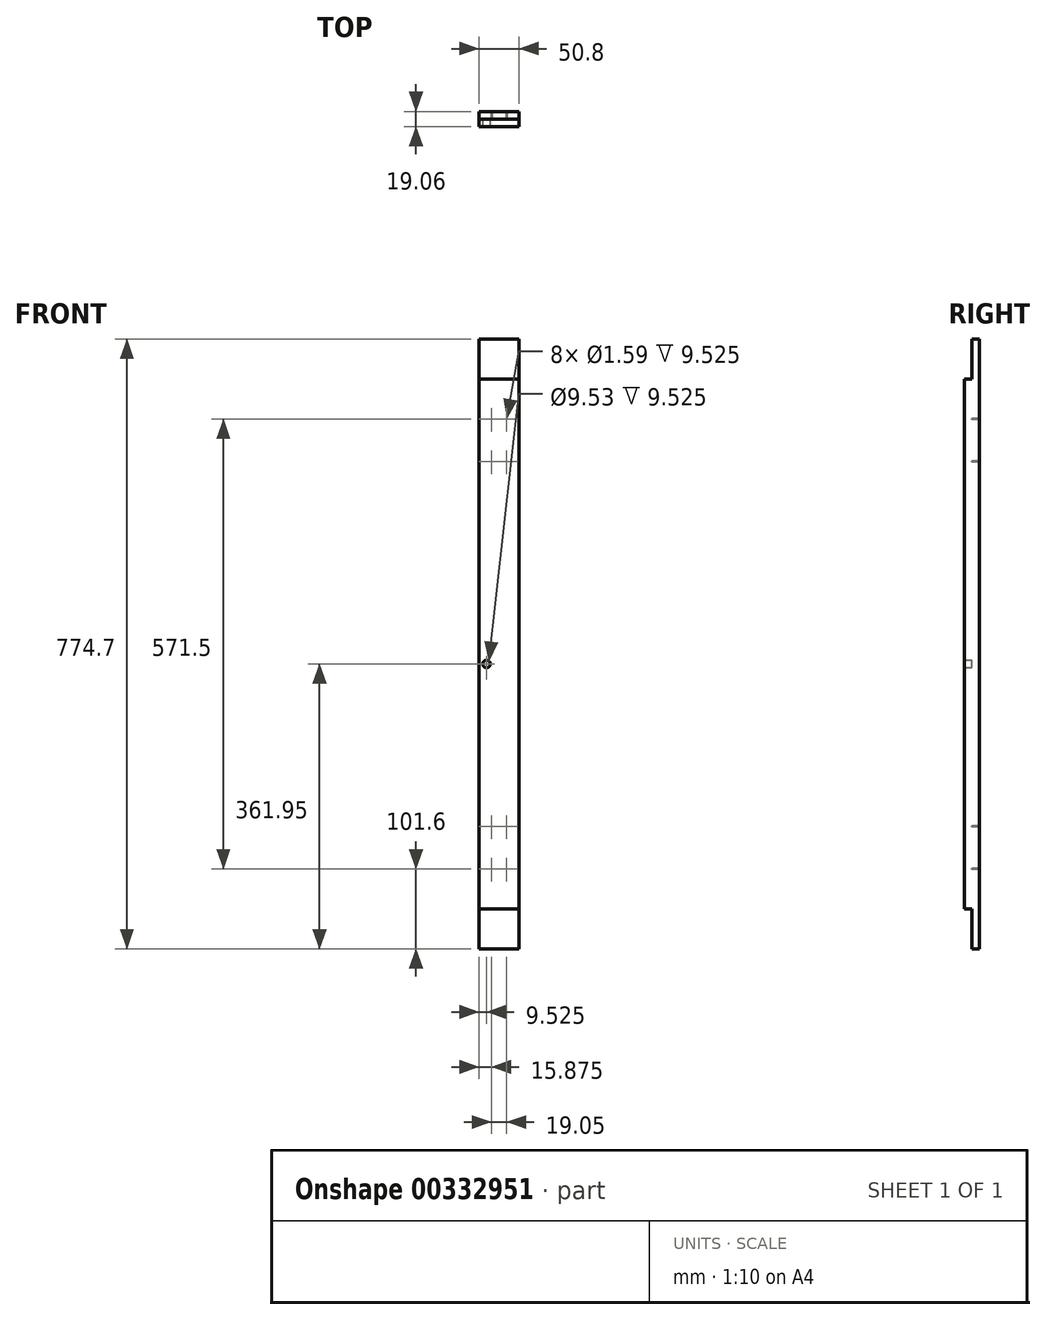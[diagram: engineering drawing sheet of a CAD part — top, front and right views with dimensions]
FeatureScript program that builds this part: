
annotation { "Feature Type Name" : "Feature", "Feature Type Description" : "" }
export const myFeature = defineFeature(function(context is Context, id is Id, definition is map)
    precondition{}
    {
        {
            var Q0;
            Q0=qCreatedBy(makeId("Top.planeOp"),FACE);
            var sketch = newSketch(context, id + "F0", { "sketchPlane" : qUnion([Q0])});
            skLineSegment(sketch, "E0.bottom", {"start": v(25.4, 9.53) * mm, "end": v(-25.4, 9.53) * mm});
            skLineSegment(sketch, "E0.top", {"start": v(25.4, -9.53) * mm, "end": v(-25.4, -9.53) * mm});
            skLineSegment(sketch, "E0.left", {"start": v(25.4, 9.53) * mm, "end": v(25.4, -9.52) * mm});
            skLineSegment(sketch, "E0.right", {"start": v(-25.4, 9.53) * mm, "end": v(-25.4, -9.53) * mm});
            skPoint(sketch, "E0.middle", {"position": v(0, 0) * mm});
            skSolve(sketch);
        }
        {
            var Q0;
            Q0=makeQuery(id+"F0.imprint","IMPRINT",FACE,{"disambiguationData":[TD([[makeQuery(id+"F0.imprint","IMPRINT",EDGE,{"derivedFrom":sQuery(id+"F0.wireOp",EDGE,"E0.bottom")}),1.0]])]});
            var Q1;
            Q1=qSketchRegion(id+"F2",true);
            extrude(context, id + "F1", {"entities" : qUnion([Q0, Q1]), "depth" : 774.7 * mm});
        }
        {
            var Q0;
            Q0=qCreatedBy(makeId("Front.planeOp"),FACE);
            var sketch = newSketch(context, id + "F2", { "sketchPlane" : qUnion([Q0])});
            skLineSegment(sketch, "E1.bottom", {"start": v(-38.77, 0) * mm, "end": v(83.66, 0) * mm});
            skLineSegment(sketch, "E1.top", {"start": v(-38.77, 50.8) * mm, "end": v(83.66, 50.8) * mm});
            skLineSegment(sketch, "E1.left", {"start": v(-38.77, 0) * mm, "end": v(-38.77, 50.8) * mm});
            skLineSegment(sketch, "E1.right", {"start": v(83.66, 0) * mm, "end": v(83.66, 50.8) * mm});
            skLineSegment(sketch, "E2.bottom", {"start": v(-210.36, 723.9) * mm, "end": v(132.8, 723.9) * mm});
            skLineSegment(sketch, "E2.top", {"start": v(-210.36, 774.7) * mm, "end": v(132.8, 774.7) * mm});
            skLineSegment(sketch, "E2.left", {"start": v(-210.36, 723.9) * mm, "end": v(-210.36, 774.7) * mm});
            skLineSegment(sketch, "E2.right", {"start": v(132.8, 723.9) * mm, "end": v(132.8, 774.7) * mm});
            skSolve(sketch);
        }
        {
            var Q0;
            Q0=qSketchRegion(id+"F2",true);
            extrude(context, id + "F3", {"entities" : qUnion([Q0]), "operationType" : NewBodyOperationType.REMOVE, "depth" : 25.4 * mm});
        }
        {
            var Q0;
            Q0=qCreatedBy(makeId("Front.planeOp"),FACE);
            var sketch = newSketch(context, id + "F4", { "sketchPlane" : qUnion([Q0])});
            skCircle(sketch, "E3", {"center": v(9.53, 101.6) * mm, "radius": 0.8 * mm});
            skCircle(sketch, "E4", {"center": v(9.52, 155.58) * mm, "radius": 0.8 * mm});
            skCircle(sketch, "E5", {"center": v(9.52, 619.12) * mm, "radius": 0.8 * mm});
            skCircle(sketch, "E6", {"center": v(9.52, 673.1) * mm, "radius": 0.8 * mm});
            skLineSegment(sketch, "E7", {"start": v(0, 0) * mm, "end": v(0, 1192.46) * mm, "construction": true});
            skLineSegment(sketch, "E8.bottom", {"start": v(9.52, 101.6) * mm, "end": v(-9.52, 101.6) * mm, "construction": true});
            skLineSegment(sketch, "E8.top", {"start": v(9.52, 673.1) * mm, "end": v(-9.53, 673.1) * mm, "construction": true});
            skLineSegment(sketch, "E8.left", {"start": v(9.53, 101.6) * mm, "end": v(9.52, 673.1) * mm, "construction": true});
            skLineSegment(sketch, "E8.right", {"start": v(-9.53, 101.6) * mm, "end": v(-9.53, 673.1) * mm, "construction": true});
            skCircle(sketch, "E9", {"center": v(-9.53, 619.12) * mm, "radius": 0.8 * mm});
            skCircle(sketch, "E10", {"center": v(-9.53, 673.1) * mm, "radius": 0.8 * mm});
            skCircle(sketch, "E11", {"center": v(-9.53, 101.6) * mm, "radius": 0.8 * mm});
            skCircle(sketch, "E12", {"center": v(-9.53, 155.58) * mm, "radius": 0.8 * mm});
            skSolve(sketch);
        }
        {
            var Q0;
            Q0=qSketchRegion(id+"F4",true);
            extrude(context, id + "F5", {"entities" : qUnion([Q0]), "operationType" : NewBodyOperationType.REMOVE, "oppositeDirection" : true, "depth" : 25.4 * mm});
        }
        {
            var Q0;
            Q0=qCreatedBy(makeId("Front.planeOp"),FACE);
            var sketch = newSketch(context, id + "F6", { "sketchPlane" : qUnion([Q0])});
            skCircle(sketch, "E13", {"center": v(-15.88, 361.95) * mm, "radius": 4.76 * mm});
            skSolve(sketch);
        }
        {
            var Q0;
            Q0=qSketchRegion(id+"F6",true);
            extrude(context, id + "F7", {"entities" : qUnion([Q0]), "operationType" : NewBodyOperationType.REMOVE, "depth" : 25.4 * mm});
        }
    });
